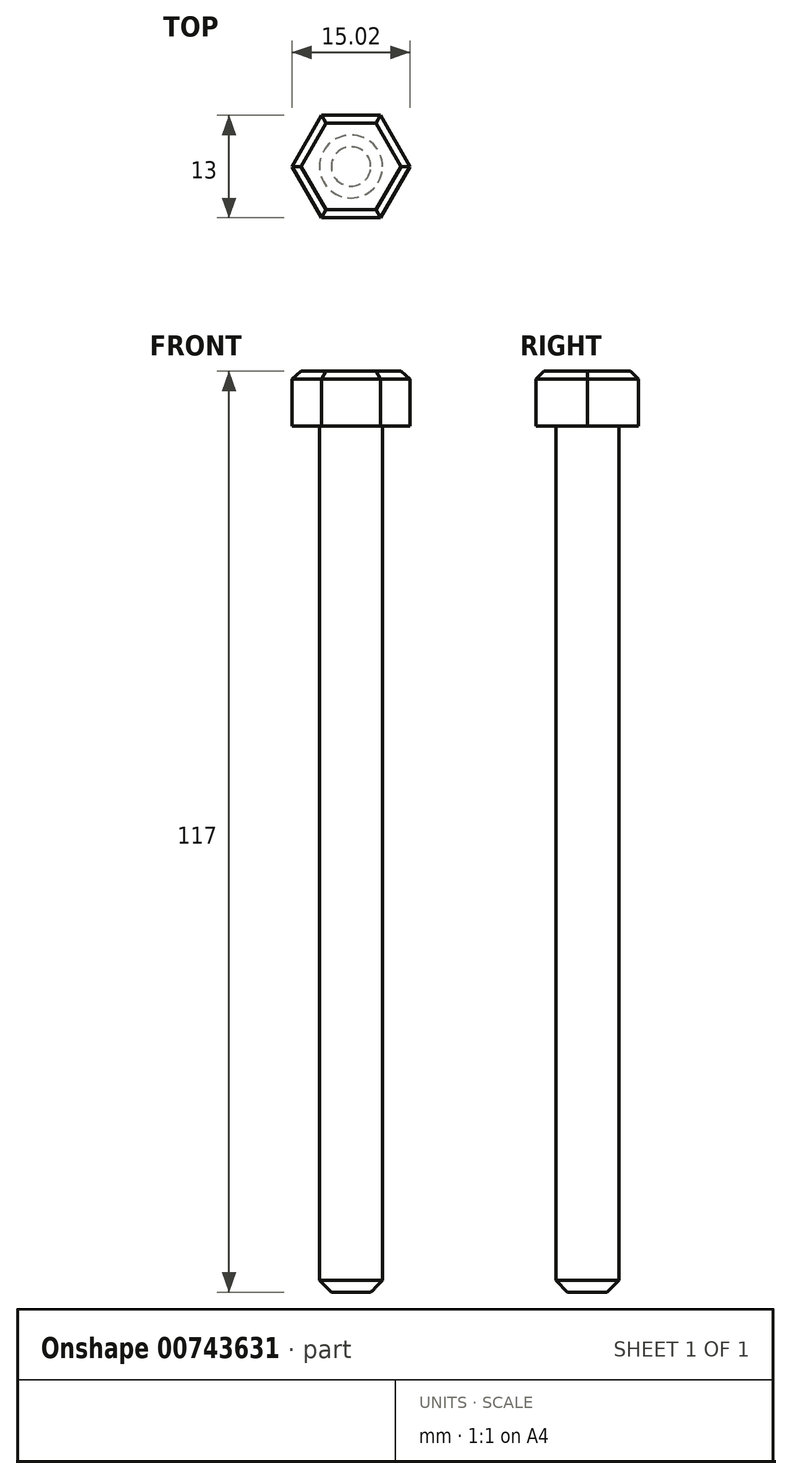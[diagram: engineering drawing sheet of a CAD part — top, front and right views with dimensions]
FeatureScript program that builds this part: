
annotation { "Feature Type Name" : "Feature", "Feature Type Description" : "" }
export const myFeature = defineFeature(function(context is Context, id is Id, definition is map)
    precondition{}
    {
        {
            var Q0;
            Q0=qCreatedBy(makeId("Top.planeOp"),FACE);
            var sketch = newSketch(context, id + "F0", { "sketchPlane" : qUnion([Q0])});
            skCircle(sketch, "E0", {"center": v(0, 0) * mm, "radius": 4 * mm});
            skCircle(sketch, "E1.cCircle", {"center": v(0, 0) * mm, "radius": 6.5 * mm, "construction": true});
            skLineSegment(sketch, "E1.0", {"start": v(-3.75, 6.5) * mm, "end": v(3.75, 6.5) * mm});
            skLineSegment(sketch, "E1.1", {"start": v(3.75, 6.5) * mm, "end": v(7.5, 0) * mm});
            skLineSegment(sketch, "E1.2", {"start": v(7.5, 0) * mm, "end": v(3.75, -6.5) * mm});
            skLineSegment(sketch, "E1.3", {"start": v(3.75, -6.5) * mm, "end": v(-3.75, -6.5) * mm});
            skLineSegment(sketch, "E1.4", {"start": v(-3.75, -6.5) * mm, "end": v(-7.5, 0) * mm});
            skLineSegment(sketch, "E1.5", {"start": v(-7.5, 0) * mm, "end": v(-3.75, 6.5) * mm});
            skPoint(sketch, "E1.0.midPoint", {"position": v(0, 6.5) * mm});
            skSolve(sketch);
        }
        {
            var Q0;
            Q0 = qSketchRegion(id + "F0", true);
            var Q1;
            Q1=makeQuery(id+"F0.imprint","IMPRINT",FACE,{"disambiguationData":[TD([[makeQuery(id+"F0.imprint","IMPRINT",EDGE,{"derivedFrom":sQuery(id+"F0.wireOp",EDGE,"E0")}),1.0]])]});
            extrude(context, id + "F1", {"entities" : qUnion([Q0, Q1]), "depth" : 7 * mm, "offsetDistance" : 25 * mm});
        }
        {
            var Q0;
            Q0=makeQuery(id+"F0.imprint","IMPRINT",FACE,{"disambiguationData":[TD([[makeQuery(id+"F0.imprint","IMPRINT",EDGE,{"derivedFrom":sQuery(id+"F0.wireOp",EDGE,"E0")}),1.0]])]});
            extrude(context, id + "F2", {"entities" : qUnion([Q0]), "operationType" : NewBodyOperationType.ADD, "oppositeDirection" : true, "depth" : 110 * mm, "offsetDistance" : 25 * mm});
        }
        {
            var Q0;
            Q0=makeQuery(id+"F2.opExtrude","CAP_EDGE",EDGE,{"disambiguationData":[OSD([sQuery(id+"F0.wireOp",EDGE,"E0")])],"isStart":false});
            chamfer(context, id + "F3", {"entities" : qUnion([Q0]), "width" : 1.5 * mm, "tangentPropagation" : true});
        }
        {
            var Q0;
            Q0=makeQuery(id+"F1.opExtrude","CAP_EDGE",EDGE,{"disambiguationData":[OSD([sQuery(id+"F0.wireOp",EDGE,"E1.1")])],"isStart":false});
            var Q1;
            Q1=makeQuery(id+"F1.opExtrude","CAP_FACE",FACE,{"disambiguationData":[OSD([sQuery(id+"F0.wireOp",EDGE,"E1.0"),sQuery(id+"F0.wireOp",EDGE,"E1.1"),sQuery(id+"F0.wireOp",EDGE,"E1.2"),sQuery(id+"F0.wireOp",EDGE,"E1.3"),sQuery(id+"F0.wireOp",EDGE,"E1.4"),sQuery(id+"F0.wireOp",EDGE,"E1.5")])],"isStart":false});
            chamfer(context, id + "F4", {"entities" : qUnion([Q0, Q1]), "chamferType" : ChamferType.TWO_OFFSETS, "width1" : 1 * mm, "oppositeDirection" : false, "width2" : 1 * mm, "tangentPropagation" : true});
        }
    });
